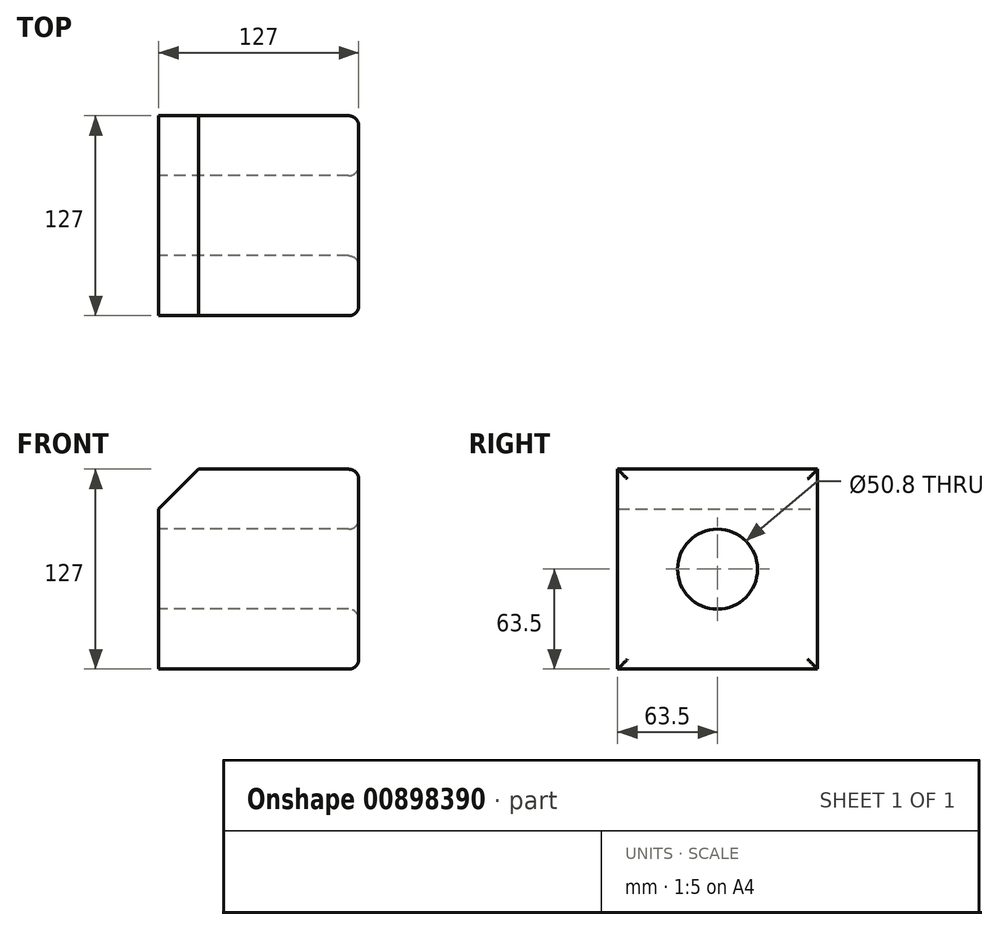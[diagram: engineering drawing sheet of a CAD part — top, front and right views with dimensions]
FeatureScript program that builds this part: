
annotation { "Feature Type Name" : "Feature", "Feature Type Description" : "" }
export const myFeature = defineFeature(function(context is Context, id is Id, definition is map)
    precondition{}
    {
        {
            var Q0;
            Q0=qCreatedBy(makeId("Front.planeOp"),FACE);
            var sketch = newSketch(context, id + "F0", { "sketchPlane" : qUnion([Q0])});
            skLineSegment(sketch, "E0.bottom", {"start": v(63.5, 63.5) * mm, "end": v(-63.5, 63.5) * mm});
            skLineSegment(sketch, "E0.top", {"start": v(63.5, -63.5) * mm, "end": v(-63.5, -63.5) * mm});
            skLineSegment(sketch, "E0.left", {"start": v(63.5, 63.5) * mm, "end": v(63.5, -63.5) * mm});
            skLineSegment(sketch, "E0.right", {"start": v(-63.5, 63.5) * mm, "end": v(-63.5, -63.5) * mm});
            skPoint(sketch, "E0.middle", {"position": v(0, 0) * mm});
            skSolve(sketch);
        }
        {
            var Q0;
            Q0 = qSketchRegion(id + "F0", true);
            extrude(context, id + "F1", {"entities" : qUnion([Q0]), "endBound" : BoundingType.SYMMETRIC, "depth" : 127 * mm, "offsetDistance" : 25.4 * mm});
        }
        {
            var Q0;
            Q0=makeQuery(id+"F1.opExtrude","SWEPT_EDGE",EDGE,{"disambiguationData":[OSD([sQuery(id+"F0.wireOp",EDGE,"E0.bottom"),sQuery(id+"F0.wireOp",EDGE,"E0.right")])]});
            chamfer(context, id + "F2", {"entities" : qUnion([Q0]), "width" : 25.4 * mm, "tangentPropagation" : true});
        }
        {
            var Q0;
            Q0=makeQuery(id+"F1.opExtrude","SWEPT_FACE",FACE,{"disambiguationData":[OSD([sQuery(id+"F0.wireOp",EDGE,"E0.right")])]});
            var sketch = newSketch(context, id + "F3", { "sketchPlane" : qUnion([Q0])});
            skCircle(sketch, "E1", {"center": v(0, 0) * mm, "radius": 25.4 * mm});
            skSolve(sketch);
        }
        {
            var Q0;
            Q0 = qSketchRegion(id + "F3", true);
            extrude(context, id + "F4", {"entities" : qUnion([Q0]), "operationType" : NewBodyOperationType.REMOVE, "endBound" : BoundingType.THROUGH_ALL, "oppositeDirection" : true, "depth" : 25.4 * mm, "offsetDistance" : 25.4 * mm});
        }
        {
            var Q0;
            Q0=makeQuery(id+"F1.opExtrude","SWEPT_FACE",FACE,{"disambiguationData":[OSD([sQuery(id+"F0.wireOp",EDGE,"E0.left")])]});
            fillet(context, id + "F5", {"entities" : qUnion([Q0]), "radius" : 6.35 * mm, "tangentPropagation" : true, "allowEdgeOverflow" : false});
        }
    });
